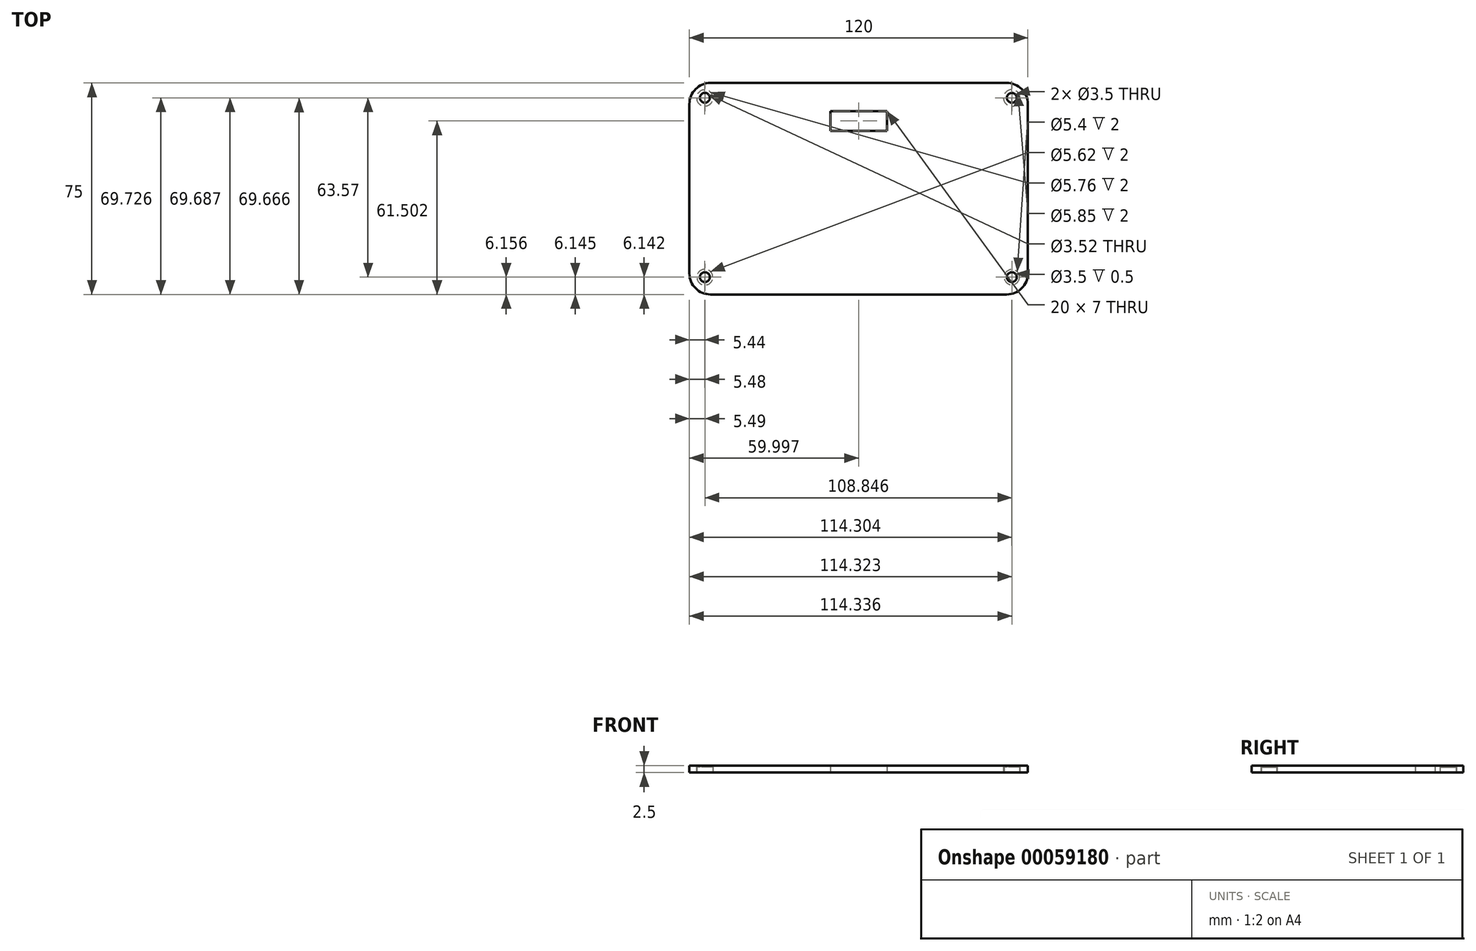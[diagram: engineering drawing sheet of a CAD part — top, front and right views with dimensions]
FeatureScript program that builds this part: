
annotation { "Feature Type Name" : "Feature", "Feature Type Description" : "" }
export const myFeature = defineFeature(function(context is Context, id is Id, definition is map)
    precondition{}
    {
        {
            var Q0;
            Q0=qCreatedBy(makeId("Top.planeOp"),FACE);
            var sketch = newSketch(context, id + "F0", { "sketchPlane" : qUnion([Q0])});
            skLineSegment(sketch, "E0.bottom", {"start": v(60.02, -37.59) * mm, "end": v(-59.98, -37.59) * mm});
            skLineSegment(sketch, "E0.top", {"start": v(60.02, 37.41) * mm, "end": v(-59.98, 37.41) * mm});
            skLineSegment(sketch, "E0.left", {"start": v(60.02, -37.59) * mm, "end": v(60.02, 37.41) * mm});
            skLineSegment(sketch, "E0.right", {"start": v(-59.98, -37.59) * mm, "end": v(-59.98, 37.41) * mm});
            skLineSegment(sketch, "E1", {"start": v(50.02, -37.59) * mm, "end": v(50.02, 37.41) * mm, "construction": true});
            skLineSegment(sketch, "E2", {"start": v(-49.98, -37.59) * mm, "end": v(-49.98, 37.41) * mm, "construction": true});
            skLineSegment(sketch, "E3", {"start": v(60.02, -27.59) * mm, "end": v(-59.98, -27.59) * mm, "construction": true});
            skLineSegment(sketch, "E4", {"start": v(60.02, 27.41) * mm, "end": v(-59.98, 27.41) * mm, "construction": true});
            skLineSegment(sketch, "E5", {"start": v(50.02, -27.59) * mm, "end": v(54.36, -27.59) * mm});
            skLineSegment(sketch, "E6", {"start": v(54.36, -27.59) * mm, "end": v(54.36, 27.41) * mm});
            skLineSegment(sketch, "E7", {"start": v(54.36, 27.41) * mm, "end": v(50.02, 27.41) * mm});
            skLineSegment(sketch, "E8", {"start": v(50.02, 27.41) * mm, "end": v(50.02, 32.14) * mm});
            skLineSegment(sketch, "E9", {"start": v(50.02, 32.14) * mm, "end": v(-49.98, 32.14) * mm});
            skLineSegment(sketch, "E10", {"start": v(-49.98, 32.14) * mm, "end": v(-49.98, 27.41) * mm});
            skLineSegment(sketch, "E11", {"start": v(-49.98, 27.41) * mm, "end": v(-54.49, 27.41) * mm});
            skLineSegment(sketch, "E12", {"start": v(-54.49, 27.41) * mm, "end": v(-54.49, -27.59) * mm});
            skLineSegment(sketch, "E13", {"start": v(-54.49, -27.59) * mm, "end": v(-49.98, -27.59) * mm});
            skLineSegment(sketch, "E14", {"start": v(-49.98, -27.59) * mm, "end": v(-49.98, -31.43) * mm});
            skLineSegment(sketch, "E15", {"start": v(-49.98, -31.43) * mm, "end": v(50.02, -31.43) * mm});
            skLineSegment(sketch, "E16", {"start": v(50.02, -31.43) * mm, "end": v(50.02, -27.59) * mm});
            skSolve(sketch);
        }
        {
            var Q0;
            Q0 = qSketchRegion(id + "F0", true);
            extrude(context, id + "F1", {"entities" : qUnion([Q0]), "depth" : 2.5 * mm});
        }
        {
            var Q0;
            Q0=makeQuery(id+"F1.opExtrude","SWEPT_EDGE",EDGE,{"disambiguationData":[OSD([sQuery(id+"F0.wireOp",EDGE,"E0.top"),sQuery(id+"F0.wireOp",EDGE,"E0.right")])]});
            var Q1;
            Q1=makeQuery(id+"F1.opExtrude","SWEPT_EDGE",EDGE,{"disambiguationData":[OSD([sQuery(id+"F0.wireOp",EDGE,"E0.bottom"),sQuery(id+"F0.wireOp",EDGE,"E0.right")])]});
            var Q2;
            Q2=makeQuery(id+"F1.opExtrude","SWEPT_EDGE",EDGE,{"disambiguationData":[OSD([sQuery(id+"F0.wireOp",EDGE,"E0.bottom"),sQuery(id+"F0.wireOp",EDGE,"E0.left")])]});
            var Q3;
            Q3=makeQuery(id+"F1.opExtrude","SWEPT_EDGE",EDGE,{"disambiguationData":[OSD([sQuery(id+"F0.wireOp",EDGE,"E0.top"),sQuery(id+"F0.wireOp",EDGE,"E0.left")])]});
            fillet(context, id + "F2", {"entities" : qUnion([Q0, Q1, Q2, Q3]), "radius" : 7.5 * mm, "tangentPropagation" : true, "allowEdgeOverflow" : false});
        }
        {
            var Q0;
            Q0=qCreatedBy(makeId("Top.planeOp"),FACE);
            var sketch = newSketch(context, id + "F3", { "sketchPlane" : qUnion([Q0])});
            skLineSegment(sketch, "E17", {"start": v(50.02, -27.59) * mm, "end": v(50.02, 37.41) * mm, "construction": true});
            skLineSegment(sketch, "E18", {"start": v(-49.98, -37.59) * mm, "end": v(-49.98, 37.41) * mm, "construction": true});
            skLineSegment(sketch, "E19", {"start": v(54.36, -27.59) * mm, "end": v(-59.98, -27.59) * mm, "construction": true});
            skLineSegment(sketch, "E20", {"start": v(54.36, 27.41) * mm, "end": v(-54.49, 27.41) * mm, "construction": true});
            skLineSegment(sketch, "E21", {"start": v(50.02, -27.59) * mm, "end": v(54.36, -27.59) * mm});
            skLineSegment(sketch, "E22", {"start": v(54.36, -27.59) * mm, "end": v(54.36, 27.41) * mm});
            skLineSegment(sketch, "E23", {"start": v(54.36, 27.41) * mm, "end": v(50.02, 27.41) * mm});
            skLineSegment(sketch, "E24", {"start": v(50.02, 27.41) * mm, "end": v(50.02, 32.14) * mm});
            skLineSegment(sketch, "E25", {"start": v(50.02, 32.14) * mm, "end": v(-49.98, 32.14) * mm});
            skLineSegment(sketch, "E26", {"start": v(-49.98, 32.14) * mm, "end": v(-49.98, 27.41) * mm});
            skLineSegment(sketch, "E27", {"start": v(-49.98, 27.41) * mm, "end": v(-54.49, 27.41) * mm});
            skLineSegment(sketch, "E28", {"start": v(-54.49, 27.41) * mm, "end": v(-54.49, -27.59) * mm});
            skLineSegment(sketch, "E29", {"start": v(-54.49, -27.59) * mm, "end": v(-49.98, -27.59) * mm});
            skLineSegment(sketch, "E30", {"start": v(-49.98, -27.59) * mm, "end": v(-49.98, -31.43) * mm});
            skLineSegment(sketch, "E31", {"start": v(-49.98, -31.43) * mm, "end": v(50.02, -31.43) * mm});
            skLineSegment(sketch, "E32", {"start": v(50.02, -31.43) * mm, "end": v(50.02, -27.59) * mm});
            skPoint(sketch, "E33.orphan", {"position": v(50.02, -37.59) * mm});
            skSolve(sketch);
        }
        {
            var Q0;
            Q0 = qSketchRegion(id + "F3", true);
            extrude(context, id + "F4", {"entities" : qUnion([Q0]), "operationType" : NewBodyOperationType.ADD, "depth" : 2.5 * mm});
        }
        {
            var Q0;
            Q0=qCreatedBy(makeId("Top.planeOp"),FACE);
            var sketch = newSketch(context, id + "F5", { "sketchPlane" : qUnion([Q0])});
            skLineSegment(sketch, "E34", {"start": v(-65.77, 32.14) * mm, "end": v(65.28, 32.14) * mm, "construction": true});
            skLineSegment(sketch, "E35", {"start": v(-59.02, -28.04) * mm, "end": v(72.68, -28.04) * mm, "construction": true});
            skLineSegment(sketch, "E36", {"start": v(-54.49, 42.33) * mm, "end": v(-54.49, -48.14) * mm, "construction": true});
            skLineSegment(sketch, "E37", {"start": v(54.36, 44.73) * mm, "end": v(54.36, -44.02) * mm, "construction": true});
            skCircle(sketch, "E38", {"center": v(-54.49, 32.14) * mm, "radius": 1.75 * mm, "construction": true});
            skCircle(sketch, "E39", {"center": v(-54.49, 32.14) * mm, "radius": 1.76 * mm});
            skCircle(sketch, "E40", {"center": v(54.36, 32.14) * mm, "radius": 1.75 * mm});
            skLineSegment(sketch, "E41", {"start": v(-65.7, -31.43) * mm, "end": v(66.5, -31.43) * mm, "construction": true});
            skCircle(sketch, "E42", {"center": v(54.36, -31.43) * mm, "radius": 1.75 * mm});
            skCircle(sketch, "E43", {"center": v(-54.49, -31.43) * mm, "radius": 1.75 * mm});
            skSolve(sketch);
        }
        {
            var Q0;
            Q0=makeQuery(id+"F0.imprint","IMPRINT",FACE,{"disambiguationData":[TD([[makeQuery(id+"F0.imprint","IMPRINT",EDGE,{"derivedFrom":sQuery(id+"F0.wireOp",EDGE,"E0.bottom")}),-1.0]])]});
            var sketch = newSketch(context, id + "F6", { "sketchPlane" : qUnion([Q0])});
            skCircle(sketch, "E44", {"center": v(54.34, -31.45) * mm, "radius": 2.7 * mm});
            skCircle(sketch, "E45", {"center": v(-54.5, -31.45) * mm, "radius": 2.81 * mm});
            skCircle(sketch, "E46", {"center": v(-54.54, 32.08) * mm, "radius": 2.88 * mm});
            skCircle(sketch, "E47", {"center": v(54.32, 32.1) * mm, "radius": 2.93 * mm});
            skSolve(sketch);
        }
        {
            var Q0;
            Q0 = qSketchRegion(id + "F6", true);
            extrude(context, id + "F7", {"entities" : qUnion([Q0]), "operationType" : NewBodyOperationType.REMOVE, "depth" : 2 * mm});
        }
        {
            var Q0;
            Q0 = qSketchRegion(id + "F5", true);
            extrude(context, id + "F8", {"entities" : qUnion([Q0]), "operationType" : NewBodyOperationType.REMOVE, "depth" : 25 * mm});
        }
        {
            var Q0;
            Q0=makeQuery(id+"F0.imprint","IMPRINT",FACE,{"disambiguationData":[TD([[makeQuery(id+"F0.imprint","IMPRINT",EDGE,{"derivedFrom":sQuery(id+"F0.wireOp",EDGE,"E5")}),1.0]])]});
            var sketch = newSketch(context, id + "F9", { "sketchPlane" : qUnion([Q0])});
            skLineSegment(sketch, "E48.bottom", {"start": v(10.02, 27.41) * mm, "end": v(-9.98, 27.41) * mm});
            skLineSegment(sketch, "E48.top", {"start": v(10.02, 20.41) * mm, "end": v(-9.98, 20.41) * mm});
            skLineSegment(sketch, "E48.left", {"start": v(10.02, 27.41) * mm, "end": v(10.02, 20.41) * mm});
            skLineSegment(sketch, "E48.right", {"start": v(-9.98, 27.41) * mm, "end": v(-9.98, 20.41) * mm});
            skSolve(sketch);
        }
        {
            var Q0;
            Q0 = qSketchRegion(id + "F9", true);
            extrude(context, id + "F10", {"entities" : qUnion([Q0]), "operationType" : NewBodyOperationType.REMOVE, "depth" : 25 * mm});
        }
    });
